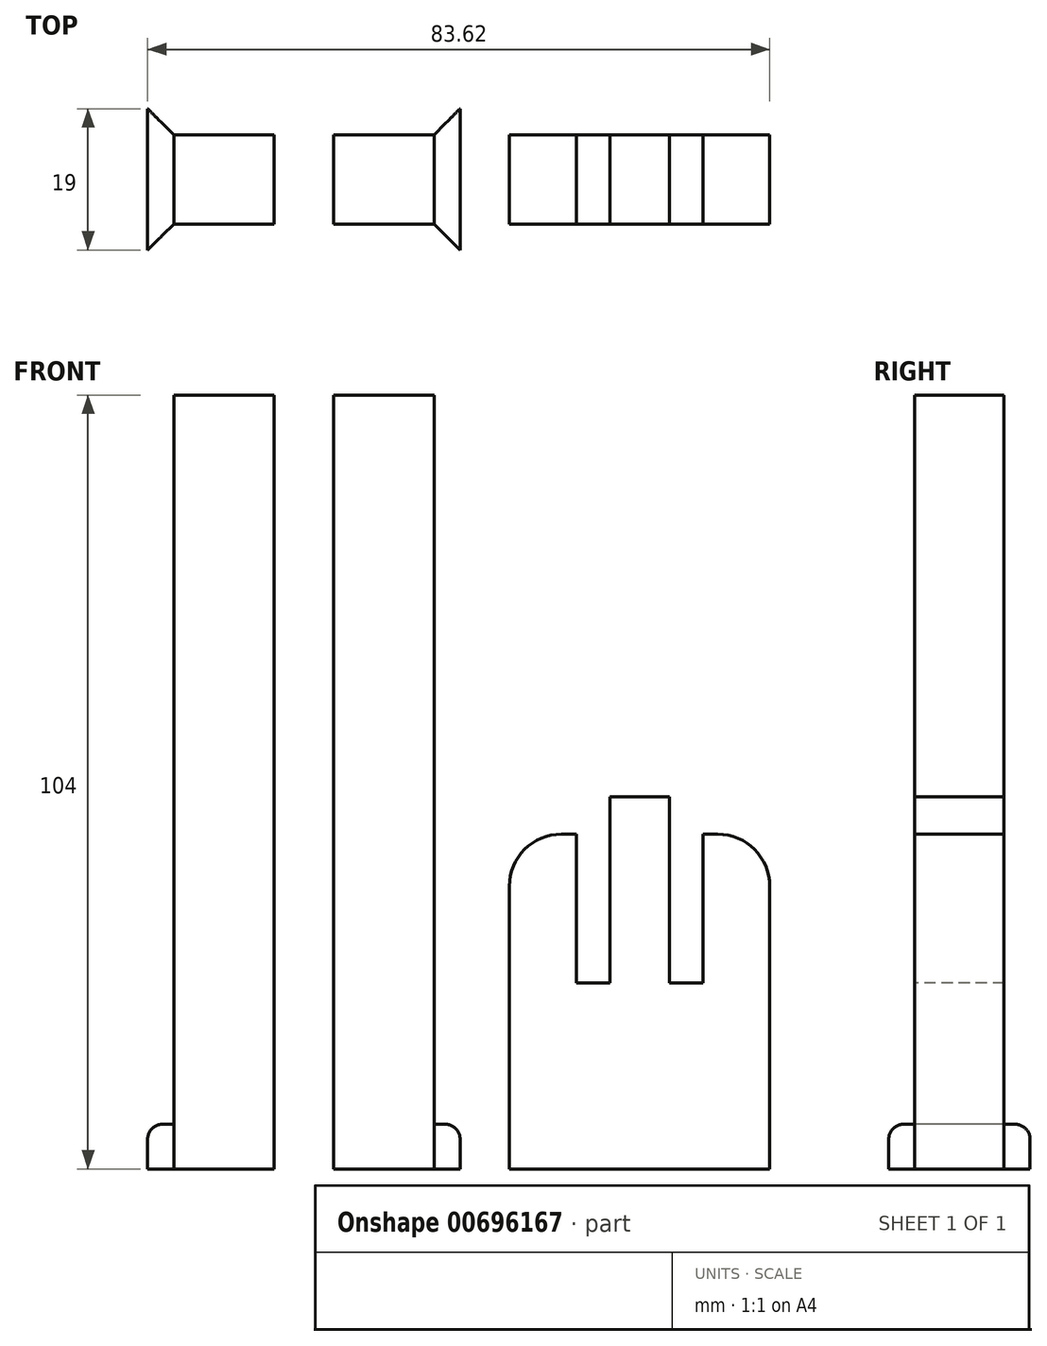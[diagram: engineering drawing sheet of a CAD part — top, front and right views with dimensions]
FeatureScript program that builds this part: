
annotation { "Feature Type Name" : "Feature", "Feature Type Description" : "" }
export const myFeature = defineFeature(function(context is Context, id is Id, definition is map)
    precondition{}
    {
        {
            var Q0;
            Q0=qCreatedBy(makeId("Top.planeOp"),FACE);
            var sketch = newSketch(context, id + "F0", { "sketchPlane" : qUnion([Q0])});
            skLineSegment(sketch, "E0.bottom", {"start": v(-17.5, 6) * mm, "end": v(17.5, 6) * mm});
            skLineSegment(sketch, "E0.top", {"start": v(-17.5, -6) * mm, "end": v(17.5, -6) * mm});
            skLineSegment(sketch, "E0.left", {"start": v(-17.5, 6) * mm, "end": v(-17.5, -6) * mm});
            skLineSegment(sketch, "E0.right", {"start": v(17.5, 6) * mm, "end": v(17.5, -6) * mm});
            skPoint(sketch, "E0.middle", {"position": v(0, 0) * mm});
            skLineSegment(sketch, "E1.bottom", {"start": v(-4, 6) * mm, "end": v(4, 6) * mm});
            skLineSegment(sketch, "E1.top", {"start": v(-4, -6) * mm, "end": v(4, -6) * mm});
            skLineSegment(sketch, "E1.left", {"start": v(-4, 6) * mm, "end": v(-4, -6) * mm});
            skLineSegment(sketch, "E1.right", {"start": v(4, 6) * mm, "end": v(4, -6) * mm});
            skLineSegment(sketch, "E2", {"start": v(-4, 6) * mm, "end": v(-8.5, 6) * mm});
            skLineSegment(sketch, "E3", {"start": v(-8.5, -6) * mm, "end": v(-8.5, 6) * mm});
            skLineSegment(sketch, "E4", {"start": v(-8.5, -6) * mm, "end": v(-4, -6) * mm});
            skLineSegment(sketch, "E5.MirrorCS", {"start": v(8.5, -6) * mm, "end": v(8.5, 6) * mm});
            skLineSegment(sketch, "E6.bottom", {"start": v(-21, 9.5) * mm, "end": v(21, 9.5) * mm});
            skLineSegment(sketch, "E6.top", {"start": v(-21, -9.5) * mm, "end": v(21, -9.5) * mm});
            skLineSegment(sketch, "E6.left", {"start": v(-21, 9.5) * mm, "end": v(-21, -9.5) * mm});
            skLineSegment(sketch, "E6.right", {"start": v(21, 9.5) * mm, "end": v(21, -9.5) * mm});
            skLineSegment(sketch, "E7", {"start": v(-21, 9.5) * mm, "end": v(-17.5, 6) * mm});
            skLineSegment(sketch, "E8", {"start": v(-17.5, -6) * mm, "end": v(-21, -9.5) * mm});
            skLineSegment(sketch, "E9", {"start": v(17.5, -6) * mm, "end": v(21, -9.5) * mm});
            skLineSegment(sketch, "E10", {"start": v(17.5, 6) * mm, "end": v(21, 9.5) * mm});
            skLineSegment(sketch, "E11.bottom", {"start": v(62.62, 6) * mm, "end": v(27.62, 6) * mm});
            skLineSegment(sketch, "E11.top", {"start": v(62.62, -6) * mm, "end": v(27.62, -6) * mm});
            skLineSegment(sketch, "E11.left", {"start": v(62.62, 6) * mm, "end": v(62.62, -6) * mm});
            skLineSegment(sketch, "E11.right", {"start": v(27.62, 6) * mm, "end": v(27.62, -6) * mm});
            skPoint(sketch, "E11.middle", {"position": v(45.12, 0) * mm});
            skLineSegment(sketch, "E12.left", {"start": v(17.5, 0) * mm, "end": v(17.5, 0) * mm});
            skPoint(sketch, "E12.middle", {"position": v(27.62, 0) * mm});
            skLineSegment(sketch, "E13.MirrorCS", {"start": v(41.12, 6) * mm, "end": v(41.12, -6) * mm});
            skLineSegment(sketch, "E14.MirrorCS", {"start": v(36.62, -6) * mm, "end": v(36.62, 6) * mm});
            skLineSegment(sketch, "E15.MirrorCS", {"start": v(49.12, 6) * mm, "end": v(49.12, -6) * mm});
            skLineSegment(sketch, "E16.MirrorCS", {"start": v(53.62, -6) * mm, "end": v(53.62, 6) * mm});
            skSolve(sketch);
        }
        {
            var Q0;
            {var subQ0=sQuery(id+"F0.wireOp",EDGE,"E0.left");Q0=makeQuery(id+"F0.imprint","IMPRINT",FACE,{"disambiguationData":[TD([[makeQuery(id+"F0.imprint","IMPRINT",EDGE,{"derivedFrom":subQ0}),1.0]])]});}
            var Q1;
            {var subQ0=sQuery(id+"F0.wireOp",EDGE,"E0.right");Q1=makeQuery(id+"F0.imprint","IMPRINT",FACE,{"disambiguationData":[TD([[makeQuery(id+"F0.imprint","IMPRINT",EDGE,{"derivedFrom":subQ0}),-1.0]])]});}
            var Q2;
            Q2=makeQuery(id+"F0.imprint","IMPRINT",FACE,{"disambiguationData":[TD([[makeQuery(id+"F0.imprint","IMPRINT",EDGE,{"derivedFrom":sQuery(id+"F0.wireOp",EDGE,"E1.left")}),-1.0]])]});
            var Q3;
            Q3=makeQuery(id+"F0.imprint","IMPRINT",FACE,{"disambiguationData":[TD([[makeQuery(id+"F0.imprint","IMPRINT",EDGE,{"derivedFrom":sQuery(id+"F0.wireOp",EDGE,"E1.bottom")}),-1.0]])]});
            var Q4;
            {var subQ0=sQuery(id+"F0.wireOp",EDGE,"E1.right");Q4=makeQuery(id+"F0.imprint","IMPRINT",FACE,{"disambiguationData":[TD([[makeQuery(id+"F0.imprint","IMPRINT",EDGE,{"derivedFrom":subQ0}),1.0]])]});}
            extrude(context, id + "F1", {"entities" : qUnion([Q0, Q1, Q2, Q3, Q4]), "depth" : 104 * mm, "offsetDistance" : 25 * mm});
        }
        {
            var Q0;
            Q0=makeQuery(id+"F0.imprint","IMPRINT",FACE,{"disambiguationData":[TD([[makeQuery(id+"F0.imprint","IMPRINT",EDGE,{"derivedFrom":sQuery(id+"F0.wireOp",EDGE,"E0.left")}),-1.0]])]});
            var Q1;
            {var subQ3=sQuery(id+"F0.wireOp",EDGE,"E1.top");Q1=makeQuery(id+"F0.imprint","IMPRINT",FACE,{"disambiguationData":[TD([[makeQuery(id+"F0.imprint","IMPRINT",EDGE,{"derivedFrom":subQ3}),-1.0]])]});}
            var Q2;
            {var subQ0=sQuery(id+"F0.wireOp",EDGE,"E1.bottom");Q2=makeQuery(id+"F0.imprint","IMPRINT",FACE,{"disambiguationData":[TD([[makeQuery(id+"F0.imprint","IMPRINT",EDGE,{"derivedFrom":subQ0}),1.0]])]});}
            var Q3;
            Q3=makeQuery(id+"F0.imprint","IMPRINT",FACE,{"disambiguationData":[TD([[makeQuery(id+"F0.imprint","IMPRINT",EDGE,{"derivedFrom":sQuery(id+"F0.wireOp",EDGE,"E0.right")}),1.0]])]});
            extrude(context, id + "F2", {"entities" : qUnion([Q0, Q1, Q2, Q3]), "operationType" : NewBodyOperationType.ADD, "depth" : 6 * mm, "offsetDistance" : 25 * mm});
        }
        {
            var Q0;
            Q0=makeQuery(id+"F2.opExtrude","CAP_EDGE",EDGE,{"disambiguationData":[OSD([sQuery(id+"F0.wireOp",EDGE,"E6.top")])],"isStart":false});
            var Q1;
            Q1=makeQuery(id+"F2.opExtrude","CAP_EDGE",EDGE,{"disambiguationData":[OSD([sQuery(id+"F0.wireOp",EDGE,"E6.right")])],"isStart":false});
            var Q2;
            Q2=makeQuery(id+"F2.opExtrude","CAP_EDGE",EDGE,{"disambiguationData":[OSD([sQuery(id+"F0.wireOp",EDGE,"E6.bottom")])],"isStart":false});
            var Q3;
            Q3=makeQuery(id+"F2.opExtrude","CAP_EDGE",EDGE,{"disambiguationData":[OSD([sQuery(id+"F0.wireOp",EDGE,"E6.left")])],"isStart":false});
            fillet(context, id + "F3", {"entities" : qUnion([Q0, Q1, Q2, Q3]), "radius" : 2 * mm, "tangentPropagation" : true, "allowEdgeOverflow" : false});
        }
        {
            var Q0;
            {var subQ0=sQuery(id+"F0.wireOp",EDGE,"E13.MirrorCS");Q0=makeQuery(id+"F0.imprint","IMPRINT",FACE,{"disambiguationData":[TD([[makeQuery(id+"F0.imprint","IMPRINT",EDGE,{"derivedFrom":subQ0}),1.0]])]});}
            extrude(context, id + "F4", {"entities" : qUnion([Q0]), "depth" : 50 * mm, "offsetDistance" : 25 * mm});
        }
        {
            var Q0;
            {var subQ0=sQuery(id+"F0.wireOp",EDGE,"E13.MirrorCS");Q0=makeQuery(id+"F0.imprint","IMPRINT",FACE,{"disambiguationData":[TD([[makeQuery(id+"F0.imprint","IMPRINT",EDGE,{"derivedFrom":subQ0}),-1.0]])]});}
            var Q1;
            {var subQ0=sQuery(id+"F0.wireOp",EDGE,"E15.MirrorCS");Q1=makeQuery(id+"F0.imprint","IMPRINT",FACE,{"disambiguationData":[TD([[makeQuery(id+"F0.imprint","IMPRINT",EDGE,{"derivedFrom":subQ0}),1.0]])]});}
            extrude(context, id + "F5", {"entities" : qUnion([Q0, Q1]), "operationType" : NewBodyOperationType.ADD, "depth" : 25 * mm, "offsetDistance" : 25 * mm});
        }
        {
            var Q0;
            {var subQ0=sQuery(id+"F0.wireOp",EDGE,"E11.right");Q0=makeQuery(id+"F0.imprint","IMPRINT",FACE,{"disambiguationData":[TD([[makeQuery(id+"F0.imprint","IMPRINT",EDGE,{"derivedFrom":subQ0}),1.0]])]});}
            var Q1;
            {var subQ0=sQuery(id+"F0.wireOp",EDGE,"E11.left");Q1=makeQuery(id+"F0.imprint","IMPRINT",FACE,{"disambiguationData":[TD([[makeQuery(id+"F0.imprint","IMPRINT",EDGE,{"derivedFrom":subQ0}),-1.0]])]});}
            extrude(context, id + "F6", {"entities" : qUnion([Q0, Q1]), "operationType" : NewBodyOperationType.ADD, "depth" : 45 * mm, "offsetDistance" : 25 * mm});
        }
        {
            var Q0;
            Q0=makeQuery(id+"F6.opExtrude","CAP_EDGE",EDGE,{"disambiguationData":[OSD([sQuery(id+"F0.wireOp",EDGE,"E11.right")])],"isStart":false});
            var Q1;
            Q1=makeQuery(id+"F6.opExtrude","CAP_EDGE",EDGE,{"disambiguationData":[OSD([sQuery(id+"F0.wireOp",EDGE,"E11.left")])],"isStart":false});
            fillet(context, id + "F7", {"entities" : qUnion([Q0, Q1]), "radius" : 7 * mm, "tangentPropagation" : true, "allowEdgeOverflow" : false});
        }
    });
